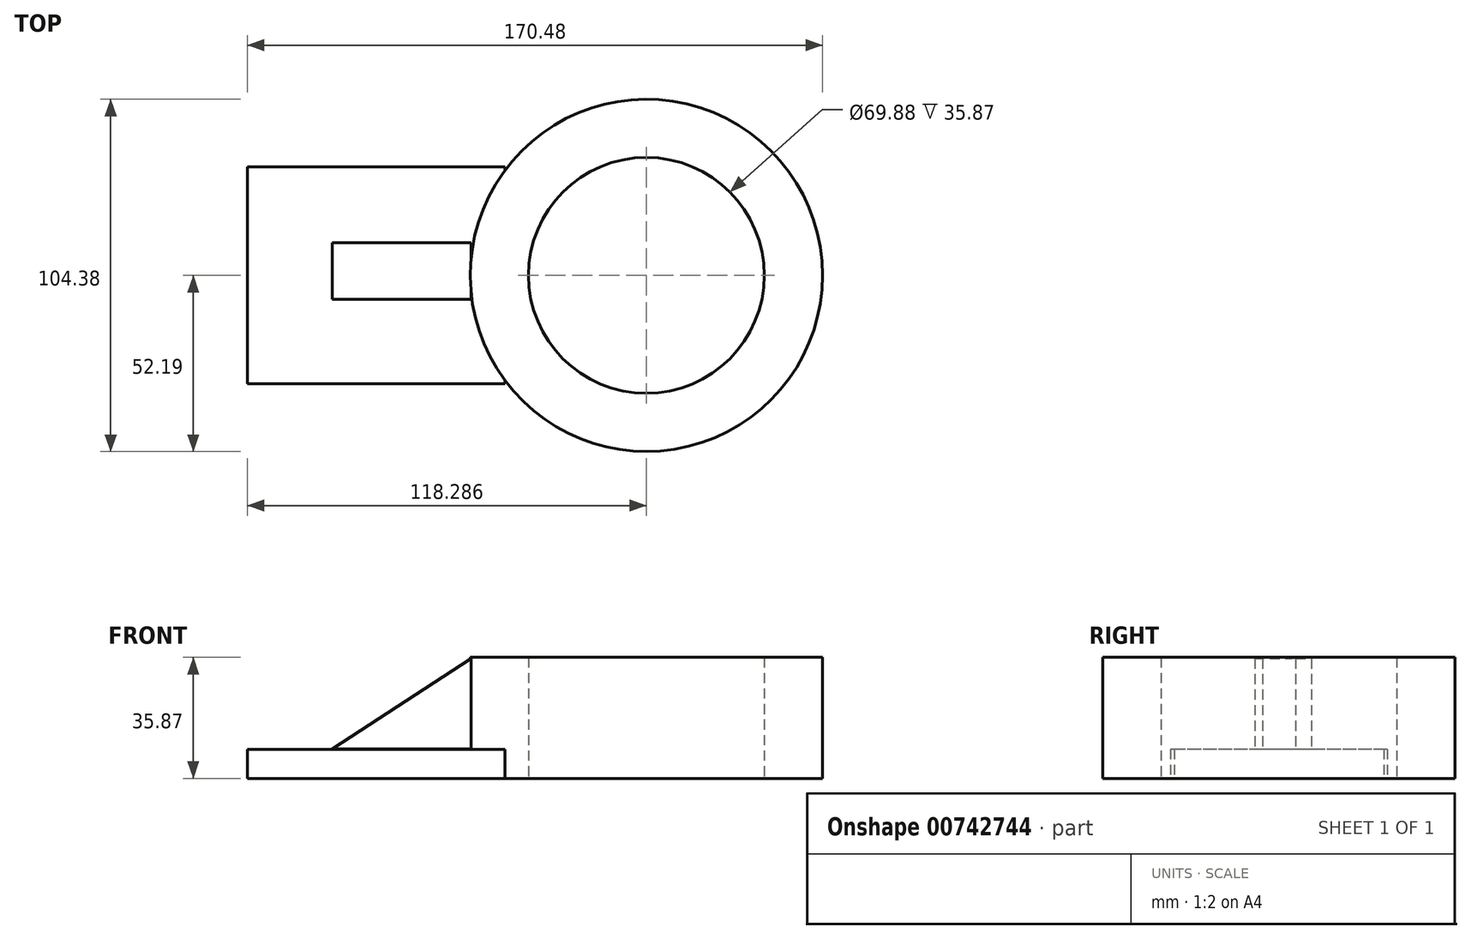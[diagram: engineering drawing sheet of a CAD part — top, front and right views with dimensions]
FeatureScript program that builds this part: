
annotation { "Feature Type Name" : "Feature", "Feature Type Description" : "" }
export const myFeature = defineFeature(function(context is Context, id is Id, definition is map)
    precondition{}
    {
        {
            var Q0;
            Q0=qCreatedBy(makeId("Top.planeOp"),FACE);
            var sketch = newSketch(context, id + "F0", { "sketchPlane" : qUnion([Q0])});
            skLineSegment(sketch, "E0.bottom", {"start": v(0, 32.16) * mm, "end": v(-76.34, 32.16) * mm});
            skLineSegment(sketch, "E0.top", {"start": v(0, -32.16) * mm, "end": v(-76.34, -32.16) * mm});
            skLineSegment(sketch, "E0.left", {"start": v(0, 32.16) * mm, "end": v(0, -32.16) * mm});
            skLineSegment(sketch, "E0.right", {"start": v(-76.34, 32.16) * mm, "end": v(-76.34, -32.16) * mm});
            skPoint(sketch, "E0.middle", {"position": v(-38.17, 0) * mm});
            skSolve(sketch);
        }
        {
            var Q0;
            Q0 = qSketchRegion(id + "F0", true);
            extrude(context, id + "F1", {"entities" : qUnion([Q0]), "depth" : 8.68 * mm, "offsetDistance" : 25.4 * mm});
        }
        {
            var Q0;
            Q0=qCreatedBy(makeId("Top.planeOp"),FACE);
            var sketch = newSketch(context, id + "F2", { "sketchPlane" : qUnion([Q0])});
            skCircle(sketch, "E1", {"center": v(41.95, 0) * mm, "radius": 52.2 * mm});
            skCircle(sketch, "E2", {"center": v(41.95, 0) * mm, "radius": 34.94 * mm});
            skSolve(sketch);
        }
        {
            var Q0;
            Q0=makeQuery(id+"F2.imprint","IMPRINT",FACE,{"disambiguationData":[TD([[makeQuery(id+"F2.imprint","IMPRINT",EDGE,{"derivedFrom":sQuery(id+"F2.wireOp",EDGE,"E1")}),1.0]])]});
            extrude(context, id + "F3", {"entities" : qUnion([Q0]), "operationType" : NewBodyOperationType.ADD, "depth" : 35.87 * mm, "offsetDistance" : 25.4 * mm});
        }
        {
            var Q0;
            Q0=qCreatedBy(makeId("Front.planeOp"),FACE);
            var sketch = newSketch(context, id + "F4", { "sketchPlane" : qUnion([Q0])});
            skLineSegment(sketch, "E3", {"start": v(-10.01, 35.53) * mm, "end": v(-10.01, 8.74) * mm});
            skLineSegment(sketch, "E4", {"start": v(-10.01, 8.74) * mm, "end": v(-51.11, 8.74) * mm});
            skLineSegment(sketch, "E5", {"start": v(-51.11, 8.74) * mm, "end": v(-10.01, 35.53) * mm});
            skSolve(sketch);
        }
        {
            var Q0;
            Q0=makeQuery(id+"F4.imprint","IMPRINT",FACE,{"disambiguationData":[TD([[makeQuery(id+"F4.imprint","IMPRINT",EDGE,{"derivedFrom":sQuery(id+"F4.wireOp",EDGE,"E3")}),-1.0]])]});
            extrude(context, id + "F5", {"entities" : qUnion([Q0]), "operationType" : NewBodyOperationType.ADD, "depth" : 7.1 * mm, "offsetDistance" : 25.4 * mm, "hasSecondDirection" : true, "secondDirectionOppositeDirection" : true, "secondDirectionDepth" : 9.7 * mm});
        }
    });
